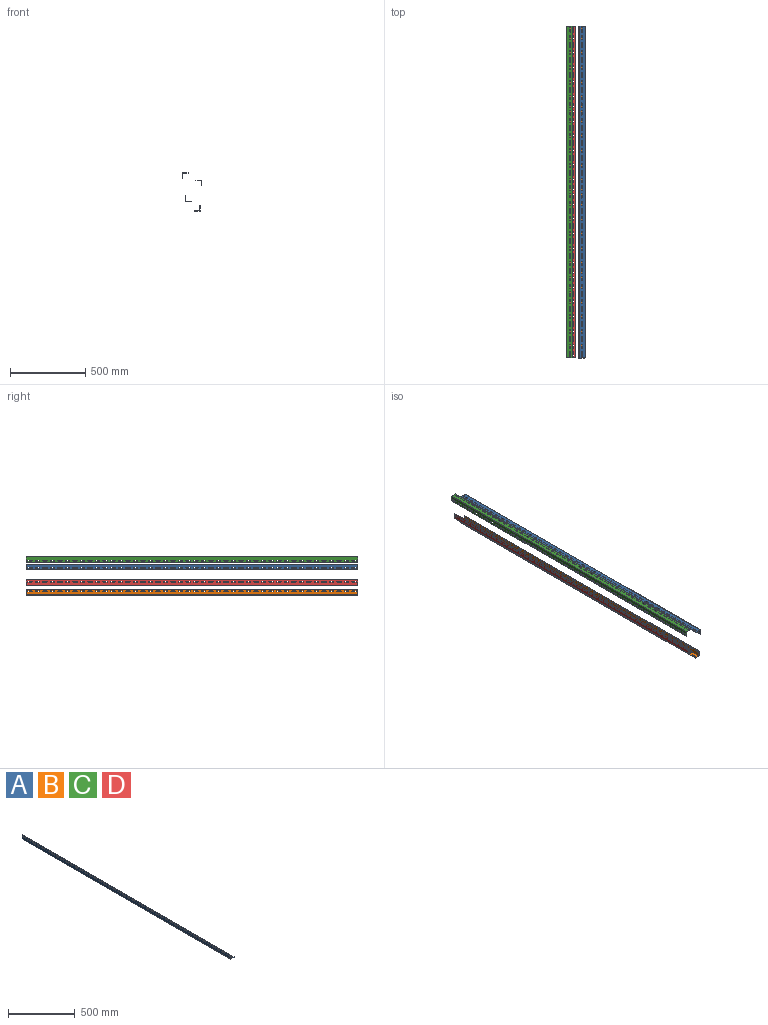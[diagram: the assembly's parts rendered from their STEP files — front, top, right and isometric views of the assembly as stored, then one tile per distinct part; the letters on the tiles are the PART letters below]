
ASSEMBLY  parts=4 mates=3
PART A: 360 faces, bbox 38.1x2200x38.1 mm
  f0: plane 2200x38.1mm, normal (-1,0,0), area 76239.9mm2, adj f1,f5,f6,f7,f184,f185,f186,f187
  f1: plane 2200x38.1mm, normal (0,0,-1), area 76239.9mm2, adj f0,f2,f6,f7,f8,f9,f10,f11
  f2: plane 2200x2mm, normal (1,0,0), area 4400mm2, adj f1,f3,f6,f7
  f3: plane 2200x36.1mm, normal (0,0,1), area 71839.9mm2, adj f2,f4,f6,f7,f8,f9,f10,f11
  f4: plane 2200x36.1mm, normal (1,0,0), area 71839.9mm2, adj f3,f5,f6,f7,f184,f185,f186,f187
  f5: plane 2200x2mm, normal (0,0,1), area 4400mm2, adj f0,f4,f6,f7
  f6: plane 38.1x38.1mm, normal (0,1,0), area 148.4mm2, adj f0,f1,f2,f3,f4,f5
  f7: plane 38.1x38.1mm, normal (0,-1,0), area 148.4mm2, adj f0,f1,f2,f3,f4,f5
  f8: cylinder r=3mm len=6mm, axis (0,0,1), area 18.8mm2, adj f1,f3,f9,f10
  f9: plane 24x2mm, normal (-1,0,0), area 48mm2, adj f1,f3,f8,f11
  f10: plane 24x2mm, normal (1,0,0), area 48mm2, adj f1,f3,f8,f11
  f11: cylinder r=3mm len=6mm, axis (0,0,1), area 18.8mm2, adj f1,f3,f9,f10
  f12: cylinder r=3mm len=6mm, axis (0,0,1), area 18.8mm2, adj f1,f3,f13,f14
  f13: plane 24x2mm, normal (-1,0,0), area 48mm2, adj f1,f3,f12,f15
  f14: plane 24x2mm, normal (1,0,0), area 48mm2, adj f1,f3,f12,f15
  f15: cylinder r=3mm len=6mm, axis (0,0,1), area 18.8mm2, adj f1,f3,f13,f14
  f16: cylinder r=3mm len=6mm, axis (0,0,1), area 18.8mm2, adj f1,f3,f17,f18
  f17: plane 24x2mm, normal (-1,0,0), area 48mm2, adj f1,f3,f16,f19
  f18: plane 24x2mm, normal (1,0,0), area 48mm2, adj f1,f3,f16,f19
  f19: cylinder r=3mm len=6mm, axis (0,0,1), area 18.8mm2, adj f1,f3,f17,f18
  f20: cylinder r=3mm len=6mm, axis (0,0,1), area 18.8mm2, adj f1,f3,f21,f22
  f21: plane 24x2mm, normal (-1,0,0), area 48mm2, adj f1,f3,f20,f23
  f22: plane 24x2mm, normal (1,0,0), area 48mm2, adj f1,f3,f20,f23
  f23: cylinder r=3mm len=6mm, axis (0,0,1), area 18.8mm2, adj f1,f3,f21,f22
  f24: cylinder r=3mm len=6mm, axis (0,0,1), area 18.8mm2, adj f1,f3,f25,f26
  f25: plane 24x2mm, normal (-1,0,0), area 48mm2, adj f1,f3,f24,f27
  f26: plane 24x2mm, normal (1,0,0), area 48mm2, adj f1,f3,f24,f27
  f27: cylinder r=3mm len=6mm, axis (0,0,1), area 18.8mm2, adj f1,f3,f25,f26
  f28: cylinder r=3mm len=6mm, axis (0,0,1), area 18.8mm2, adj f1,f3,f29,f30
  f29: plane 24x2mm, normal (-1,0,0), area 48mm2, adj f1,f3,f28,f31
  f30: plane 24x2mm, normal (1,0,0), area 48mm2, adj f1,f3,f28,f31
  f31: cylinder r=3mm len=6mm, axis (0,0,1), area 18.8mm2, adj f1,f3,f29,f30
  f32: cylinder r=3mm len=6mm, axis (0,0,1), area 18.8mm2, adj f1,f3,f33,f34
  f33: plane 24x2mm, normal (-1,0,0), area 48mm2, adj f1,f3,f32,f35
  f34: plane 24x2mm, normal (1,0,0), area 48mm2, adj f1,f3,f32,f35
  f35: cylinder r=3mm len=6mm, axis (0,0,1), area 18.8mm2, adj f1,f3,f33,f34
  f36: cylinder r=3mm len=6mm, axis (0,0,1), area 18.8mm2, adj f1,f3,f37,f38
  f37: plane 24x2mm, normal (-1,0,0), area 48mm2, adj f1,f3,f36,f39
  f38: plane 24x2mm, normal (1,0,0), area 48mm2, adj f1,f3,f36,f39
  f39: cylinder r=3mm len=6mm, axis (0,0,1), area 18.8mm2, adj f1,f3,f37,f38
  f40: cylinder r=3mm len=6mm, axis (0,0,1), area 18.8mm2, adj f1,f3,f41,f42
  f41: plane 24x2mm, normal (-1,0,0), area 48mm2, adj f1,f3,f40,f43
  f42: plane 24x2mm, normal (1,0,0), area 48mm2, adj f1,f3,f40,f43
  f43: cylinder r=3mm len=6mm, axis (0,0,1), area 18.8mm2, adj f1,f3,f41,f42
  f44: cylinder r=3mm len=6mm, axis (0,0,1), area 18.8mm2, adj f1,f3,f45,f46
  f45: plane 24x2mm, normal (-1,0,0), area 48mm2, adj f1,f3,f44,f47
  f46: plane 24x2mm, normal (1,0,0), area 48mm2, adj f1,f3,f44,f47
  f47: cylinder r=3mm len=6mm, axis (0,0,1), area 18.8mm2, adj f1,f3,f45,f46
  f48: cylinder r=3mm len=6mm, axis (0,0,1), area 18.8mm2, adj f1,f3,f49,f50
  f49: plane 24x2mm, normal (-1,0,0), area 48mm2, adj f1,f3,f48,f51
  f50: plane 24x2mm, normal (1,0,0), area 48mm2, adj f1,f3,f48,f51
  f51: cylinder r=3mm len=6mm, axis (0,0,1), area 18.8mm2, adj f1,f3,f49,f50
  f52: cylinder r=3mm len=6mm, axis (0,0,1), area 18.8mm2, adj f1,f3,f53,f54
  f53: plane 24x2mm, normal (-1,0,0), area 48mm2, adj f1,f3,f52,f55
  f54: plane 24x2mm, normal (1,0,0), area 48mm2, adj f1,f3,f52,f55
  f55: cylinder r=3mm len=6mm, axis (0,0,1), area 18.8mm2, adj f1,f3,f53,f54
  f56: cylinder r=3mm len=6mm, axis (0,0,1), area 18.8mm2, adj f1,f3,f57,f58
  f57: plane 24x2mm, normal (-1,0,0), area 48mm2, adj f1,f3,f56,f59
  f58: plane 24x2mm, normal (1,0,0), area 48mm2, adj f1,f3,f56,f59
  f59: cylinder r=3mm len=6mm, axis (0,0,1), area 18.8mm2, adj f1,f3,f57,f58
  f60: cylinder r=3mm len=6mm, axis (0,0,1), area 18.8mm2, adj f1,f3,f61,f62
  f61: plane 24x2mm, normal (-1,0,0), area 48mm2, adj f1,f3,f60,f63
  f62: plane 24x2mm, normal (1,0,0), area 48mm2, adj f1,f3,f60,f63
  f63: cylinder r=3mm len=6mm, axis (0,0,1), area 18.8mm2, adj f1,f3,f61,f62
  f64: cylinder r=3mm len=6mm, axis (0,0,1), area 18.8mm2, adj f1,f3,f65,f66
  f65: plane 24x2mm, normal (-1,0,0), area 48mm2, adj f1,f3,f64,f67
  f66: plane 24x2mm, normal (1,0,0), area 48mm2, adj f1,f3,f64,f67
  f67: cylinder r=3mm len=6mm, axis (0,0,1), area 18.8mm2, adj f1,f3,f65,f66
  f68: cylinder r=3mm len=6mm, axis (0,0,1), area 18.8mm2, adj f1,f3,f69,f70
  f69: plane 24x2mm, normal (-1,0,0), area 48mm2, adj f1,f3,f68,f71
  f70: plane 24x2mm, normal (1,0,0), area 48mm2, adj f1,f3,f68,f71
  f71: cylinder r=3mm len=6mm, axis (0,0,1), area 18.8mm2, adj f1,f3,f69,f70
  f72: cylinder r=3mm len=6mm, axis (0,0,1), area 18.8mm2, adj f1,f3,f73,f74
  f73: plane 24x2mm, normal (-1,0,0), area 48mm2, adj f1,f3,f72,f75
  f74: plane 24x2mm, normal (1,0,0), area 48mm2, adj f1,f3,f72,f75
  f75: cylinder r=3mm len=6mm, axis (0,0,1), area 18.8mm2, adj f1,f3,f73,f74
  f76: cylinder r=3mm len=6mm, axis (0,0,1), area 18.8mm2, adj f1,f3,f77,f78
  f77: plane 24x2mm, normal (-1,0,0), area 48mm2, adj f1,f3,f76,f79
  f78: plane 24x2mm, normal (1,0,0), area 48mm2, adj f1,f3,f76,f79
  f79: cylinder r=3mm len=6mm, axis (0,0,1), area 18.8mm2, adj f1,f3,f77,f78
  f80: cylinder r=3mm len=6mm, axis (0,0,1), area 18.8mm2, adj f1,f3,f81,f82
  f81: plane 24x2mm, normal (-1,0,0), area 48mm2, adj f1,f3,f80,f83
  f82: plane 24x2mm, normal (1,0,0), area 48mm2, adj f1,f3,f80,f83
  f83: cylinder r=3mm len=6mm, axis (0,0,1), area 18.8mm2, adj f1,f3,f81,f82
  f84: cylinder r=3mm len=6mm, axis (0,0,1), area 18.8mm2, adj f1,f3,f85,f86
  f85: plane 24x2mm, normal (-1,0,0), area 48mm2, adj f1,f3,f84,f87
  f86: plane 24x2mm, normal (1,0,0), area 48mm2, adj f1,f3,f84,f87
  f87: cylinder r=3mm len=6mm, axis (0,0,1), area 18.8mm2, adj f1,f3,f85,f86
  f88: cylinder r=3mm len=6mm, axis (0,0,1), area 18.8mm2, adj f1,f3,f89,f90
  f89: plane 24x2mm, normal (-1,0,0), area 48mm2, adj f1,f3,f88,f91
  f90: plane 24x2mm, normal (1,0,0), area 48mm2, adj f1,f3,f88,f91
  f91: cylinder r=3mm len=6mm, axis (0,0,1), area 18.8mm2, adj f1,f3,f89,f90
  f92: cylinder r=3mm len=6mm, axis (0,0,1), area 18.8mm2, adj f1,f3,f93,f94
  f93: plane 24x2mm, normal (-1,0,0), area 48mm2, adj f1,f3,f92,f95
  f94: plane 24x2mm, normal (1,0,0), area 48mm2, adj f1,f3,f92,f95
  f95: cylinder r=3mm len=6mm, axis (0,0,1), area 18.8mm2, adj f1,f3,f93,f94
  f96: cylinder r=3mm len=6mm, axis (0,0,1), area 18.8mm2, adj f1,f3,f97,f98
  f97: plane 24x2mm, normal (-1,0,0), area 48mm2, adj f1,f3,f96,f99
  f98: plane 24x2mm, normal (1,0,0), area 48mm2, adj f1,f3,f96,f99
  f99: cylinder r=3mm len=6mm, axis (0,0,1), area 18.8mm2, adj f1,f3,f97,f98
  f100: cylinder r=3mm len=6mm, axis (0,0,1), area 18.8mm2, adj f1,f3,f101,f102
  f101: plane 24x2mm, normal (-1,0,0), area 48mm2, adj f1,f3,f100,f103
  f102: plane 24x2mm, normal (1,0,0), area 48mm2, adj f1,f3,f100,f103
  f103: cylinder r=3mm len=6mm, axis (0,0,1), area 18.8mm2, adj f1,f3,f101,f102
  f104: cylinder r=3mm len=6mm, axis (0,0,1), area 18.8mm2, adj f1,f3,f105,f106
  f105: plane 24x2mm, normal (-1,0,0), area 48mm2, adj f1,f3,f104,f107
  f106: plane 24x2mm, normal (1,0,0), area 48mm2, adj f1,f3,f104,f107
  f107: cylinder r=3mm len=6mm, axis (0,0,1), area 18.8mm2, adj f1,f3,f105,f106
  f108: cylinder r=3mm len=6mm, axis (0,0,1), area 18.8mm2, adj f1,f3,f109,f110
  f109: plane 24x2mm, normal (-1,0,0), area 48mm2, adj f1,f3,f108,f111
  f110: plane 24x2mm, normal (1,0,0), area 48mm2, adj f1,f3,f108,f111
  f111: cylinder r=3mm len=6mm, axis (0,0,1), area 18.8mm2, adj f1,f3,f109,f110
  f112: cylinder r=3mm len=6mm, axis (0,0,1), area 18.8mm2, adj f1,f3,f113,f114
  f113: plane 24x2mm, normal (-1,0,0), area 48mm2, adj f1,f3,f112,f115
  f114: plane 24x2mm, normal (1,0,0), area 48mm2, adj f1,f3,f112,f115
  f115: cylinder r=3mm len=6mm, axis (0,0,1), area 18.8mm2, adj f1,f3,f113,f114
  f116: cylinder r=3mm len=6mm, axis (0,0,1), area 18.8mm2, adj f1,f3,f117,f118
  f117: plane 24x2mm, normal (-1,0,0), area 48mm2, adj f1,f3,f116,f119
  f118: plane 24x2mm, normal (1,0,0), area 48mm2, adj f1,f3,f116,f119
  f119: cylinder r=3mm len=6mm, axis (0,0,1), area 18.8mm2, adj f1,f3,f117,f118
  f120: cylinder r=3mm len=6mm, axis (0,0,1), area 18.8mm2, adj f1,f3,f121,f122
  f121: plane 24x2mm, normal (-1,0,0), area 48mm2, adj f1,f3,f120,f123
  f122: plane 24x2mm, normal (1,0,0), area 48mm2, adj f1,f3,f120,f123
  f123: cylinder r=3mm len=6mm, axis (0,0,1), area 18.8mm2, adj f1,f3,f121,f122
  f124: cylinder r=3mm len=6mm, axis (0,0,1), area 18.8mm2, adj f1,f3,f125,f126
  f125: plane 24x2mm, normal (-1,0,0), area 48mm2, adj f1,f3,f124,f127
  f126: plane 24x2mm, normal (1,0,0), area 48mm2, adj f1,f3,f124,f127
  f127: cylinder r=3mm len=6mm, axis (0,0,1), area 18.8mm2, adj f1,f3,f125,f126
  f128: cylinder r=3mm len=6mm, axis (0,0,1), area 18.8mm2, adj f1,f3,f129,f130
  f129: plane 24x2mm, normal (-1,0,0), area 48mm2, adj f1,f3,f128,f131
  f130: plane 24x2mm, normal (1,0,0), area 48mm2, adj f1,f3,f128,f131
  f131: cylinder r=3mm len=6mm, axis (0,0,1), area 18.8mm2, adj f1,f3,f129,f130
  f132: cylinder r=3mm len=6mm, axis (0,0,1), area 18.8mm2, adj f1,f3,f133,f134
  f133: plane 24x2mm, normal (-1,0,0), area 48mm2, adj f1,f3,f132,f135
  f134: plane 24x2mm, normal (1,0,0), area 48mm2, adj f1,f3,f132,f135
  f135: cylinder r=3mm len=6mm, axis (0,0,1), area 18.8mm2, adj f1,f3,f133,f134
  f136: cylinder r=3mm len=6mm, axis (0,0,1), area 18.8mm2, adj f1,f3,f137,f138
  f137: plane 24x2mm, normal (-1,0,0), area 48mm2, adj f1,f3,f136,f139
  f138: plane 24x2mm, normal (1,0,0), area 48mm2, adj f1,f3,f136,f139
  f139: cylinder r=3mm len=6mm, axis (0,0,1), area 18.8mm2, adj f1,f3,f137,f138
  f140: cylinder r=3mm len=6mm, axis (0,0,1), area 18.8mm2, adj f1,f3,f141,f142
  f141: plane 24x2mm, normal (-1,0,0), area 48mm2, adj f1,f3,f140,f143
  f142: plane 24x2mm, normal (1,0,0), area 48mm2, adj f1,f3,f140,f143
  f143: cylinder r=3mm len=6mm, axis (0,0,1), area 18.8mm2, adj f1,f3,f141,f142
  f144: cylinder r=3mm len=6mm, axis (0,0,1), area 18.8mm2, adj f1,f3,f145,f146
  f145: plane 24x2mm, normal (-1,0,0), area 48mm2, adj f1,f3,f144,f147
  f146: plane 24x2mm, normal (1,0,0), area 48mm2, adj f1,f3,f144,f147
  f147: cylinder r=3mm len=6mm, axis (0,0,1), area 18.8mm2, adj f1,f3,f145,f146
  f148: cylinder r=3mm len=6mm, axis (0,0,1), area 18.8mm2, adj f1,f3,f149,f150
  f149: plane 24x2mm, normal (-1,0,0), area 48mm2, adj f1,f3,f148,f151
  f150: plane 24x2mm, normal (1,0,0), area 48mm2, adj f1,f3,f148,f151
  f151: cylinder r=3mm len=6mm, axis (0,0,1), area 18.8mm2, adj f1,f3,f149,f150
  f152: cylinder r=3mm len=6mm, axis (0,0,1), area 18.8mm2, adj f1,f3,f153,f154
  f153: plane 24x2mm, normal (-1,0,0), area 48mm2, adj f1,f3,f152,f155
  f154: plane 24x2mm, normal (1,0,0), area 48mm2, adj f1,f3,f152,f155
  f155: cylinder r=3mm len=6mm, axis (0,0,1), area 18.8mm2, adj f1,f3,f153,f154
  f156: cylinder r=3mm len=6mm, axis (0,0,1), area 18.8mm2, adj f1,f3,f157,f158
  f157: plane 24x2mm, normal (-1,0,0), area 48mm2, adj f1,f3,f156,f159
  f158: plane 24x2mm, normal (1,0,0), area 48mm2, adj f1,f3,f156,f159
  f159: cylinder r=3mm len=6mm, axis (0,0,1), area 18.8mm2, adj f1,f3,f157,f158
  f160: cylinder r=3mm len=6mm, axis (0,0,1), area 18.8mm2, adj f1,f3,f161,f162
  f161: plane 24x2mm, normal (-1,0,0), area 48mm2, adj f1,f3,f160,f163
  f162: plane 24x2mm, normal (1,0,0), area 48mm2, adj f1,f3,f160,f163
  f163: cylinder r=3mm len=6mm, axis (0,0,1), area 18.8mm2, adj f1,f3,f161,f162
  f164: cylinder r=3mm len=6mm, axis (0,0,1), area 18.8mm2, adj f1,f3,f165,f166
  f165: plane 24x2mm, normal (-1,0,0), area 48mm2, adj f1,f3,f164,f167
  f166: plane 24x2mm, normal (1,0,0), area 48mm2, adj f1,f3,f164,f167
  f167: cylinder r=3mm len=6mm, axis (0,0,1), area 18.8mm2, adj f1,f3,f165,f166
  f168: cylinder r=3mm len=6mm, axis (0,0,1), area 18.8mm2, adj f1,f3,f169,f170
  f169: plane 24x2mm, normal (-1,0,0), area 48mm2, adj f1,f3,f168,f171
  f170: plane 24x2mm, normal (1,0,0), area 48mm2, adj f1,f3,f168,f171
  f171: cylinder r=3mm len=6mm, axis (0,0,1), area 18.8mm2, adj f1,f3,f169,f170
  f172: cylinder r=3mm len=6mm, axis (0,0,1), area 18.8mm2, adj f1,f3,f173,f174
  f173: plane 24x2mm, normal (-1,0,0), area 48mm2, adj f1,f3,f172,f175
  f174: plane 24x2mm, normal (1,0,0), area 48mm2, adj f1,f3,f172,f175
  f175: cylinder r=3mm len=6mm, axis (0,0,1), area 18.8mm2, adj f1,f3,f173,f174
  f176: cylinder r=3mm len=6mm, axis (0,0,1), area 18.8mm2, adj f1,f3,f177,f178
  f177: plane 24x2mm, normal (-1,0,0), area 48mm2, adj f1,f3,f176,f179
  f178: plane 24x2mm, normal (1,0,0), area 48mm2, adj f1,f3,f176,f179
  f179: cylinder r=3mm len=6mm, axis (0,0,1), area 18.8mm2, adj f1,f3,f177,f178
  f180: cylinder r=3mm len=6mm, axis (0,0,1), area 18.8mm2, adj f1,f3,f181,f182
  f181: plane 24x2mm, normal (-1,0,0), area 48mm2, adj f1,f3,f180,f183
  f182: plane 24x2mm, normal (1,0,0), area 48mm2, adj f1,f3,f180,f183
  f183: cylinder r=3mm len=6mm, axis (0,0,1), area 18.8mm2, adj f1,f3,f181,f182
  f184: cylinder r=3mm len=6mm, axis (1,0,0), area 18.8mm2, adj f0,f4,f185,f186
  f185: plane 24x2mm, normal (0,0,1), area 48mm2, adj f0,f4,f184,f187
  f186: plane 24x2mm, normal (0,0,-1), area 48mm2, adj f0,f4,f184,f187
  f187: cylinder r=3mm len=6mm, axis (1,0,0), area 18.8mm2, adj f0,f4,f185,f186
  f188: cylinder r=3mm len=6mm, axis (1,0,0), area 18.8mm2, adj f0,f4,f189,f190
  f189: plane 24x2mm, normal (0,0,1), area 48mm2, adj f0,f4,f188,f191
  f190: plane 24x2mm, normal (0,0,-1), area 48mm2, adj f0,f4,f188,f191
  f191: cylinder r=3mm len=6mm, axis (1,0,0), area 18.8mm2, adj f0,f4,f189,f190
  f192: cylinder r=3mm len=6mm, axis (1,0,0), area 18.8mm2, adj f0,f4,f193,f194
  f193: plane 24x2mm, normal (0,0,1), area 48mm2, adj f0,f4,f192,f195
  f194: plane 24x2mm, normal (0,0,-1), area 48mm2, adj f0,f4,f192,f195
  f195: cylinder r=3mm len=6mm, axis (1,0,0), area 18.8mm2, adj f0,f4,f193,f194
  f196: cylinder r=3mm len=6mm, axis (1,0,0), area 18.8mm2, adj f0,f4,f197,f198
  f197: plane 24x2mm, normal (0,0,1), area 48mm2, adj f0,f4,f196,f199
  f198: plane 24x2mm, normal (0,0,-1), area 48mm2, adj f0,f4,f196,f199
  f199: cylinder r=3mm len=6mm, axis (1,0,0), area 18.8mm2, adj f0,f4,f197,f198
  f200: cylinder r=3mm len=6mm, axis (1,0,0), area 18.8mm2, adj f0,f4,f201,f202
  f201: plane 24x2mm, normal (0,0,1), area 48mm2, adj f0,f4,f200,f203
  f202: plane 24x2mm, normal (0,0,-1), area 48mm2, adj f0,f4,f200,f203
  f203: cylinder r=3mm len=6mm, axis (1,0,0), area 18.8mm2, adj f0,f4,f201,f202
  f204: cylinder r=3mm len=6mm, axis (1,0,0), area 18.8mm2, adj f0,f4,f205,f206
  f205: plane 24x2mm, normal (0,0,1), area 48mm2, adj f0,f4,f204,f207
  f206: plane 24x2mm, normal (0,0,-1), area 48mm2, adj f0,f4,f204,f207
  f207: cylinder r=3mm len=6mm, axis (1,0,0), area 18.8mm2, adj f0,f4,f205,f206
  f208: cylinder r=3mm len=6mm, axis (1,0,0), area 18.8mm2, adj f0,f4,f209,f210
  f209: plane 24x2mm, normal (0,0,1), area 48mm2, adj f0,f4,f208,f211
  f210: plane 24x2mm, normal (0,0,-1), area 48mm2, adj f0,f4,f208,f211
  f211: cylinder r=3mm len=6mm, axis (1,0,0), area 18.8mm2, adj f0,f4,f209,f210
  f212: cylinder r=3mm len=6mm, axis (1,0,0), area 18.8mm2, adj f0,f4,f213,f214
  f213: plane 24x2mm, normal (0,0,1), area 48mm2, adj f0,f4,f212,f215
  f214: plane 24x2mm, normal (0,0,-1), area 48mm2, adj f0,f4,f212,f215
  f215: cylinder r=3mm len=6mm, axis (1,0,0), area 18.8mm2, adj f0,f4,f213,f214
  f216: cylinder r=3mm len=6mm, axis (1,0,0), area 18.8mm2, adj f0,f4,f217,f218
  f217: plane 24x2mm, normal (0,0,1), area 48mm2, adj f0,f4,f216,f219
  f218: plane 24x2mm, normal (0,0,-1), area 48mm2, adj f0,f4,f216,f219
  f219: cylinder r=3mm len=6mm, axis (1,0,0), area 18.8mm2, adj f0,f4,f217,f218
  f220: cylinder r=3mm len=6mm, axis (1,0,0), area 18.8mm2, adj f0,f4,f221,f222
  f221: plane 24x2mm, normal (0,0,1), area 48mm2, adj f0,f4,f220,f223
  f222: plane 24x2mm, normal (0,0,-1), area 48mm2, adj f0,f4,f220,f223
  f223: cylinder r=3mm len=6mm, axis (1,0,0), area 18.8mm2, adj f0,f4,f221,f222
  f224: cylinder r=3mm len=6mm, axis (1,0,0), area 18.8mm2, adj f0,f4,f225,f226
  f225: plane 24x2mm, normal (0,0,1), area 48mm2, adj f0,f4,f224,f227
  f226: plane 24x2mm, normal (0,0,-1), area 48mm2, adj f0,f4,f224,f227
  f227: cylinder r=3mm len=6mm, axis (1,0,0), area 18.8mm2, adj f0,f4,f225,f226
  f228: cylinder r=3mm len=6mm, axis (1,0,0), area 18.8mm2, adj f0,f4,f229,f230
  f229: plane 24x2mm, normal (0,0,1), area 48mm2, adj f0,f4,f228,f231
  f230: plane 24x2mm, normal (0,0,-1), area 48mm2, adj f0,f4,f228,f231
  f231: cylinder r=3mm len=6mm, axis (1,0,0), area 18.8mm2, adj f0,f4,f229,f230
  f232: cylinder r=3mm len=6mm, axis (1,0,0), area 18.8mm2, adj f0,f4,f233,f234
  f233: plane 24x2mm, normal (0,0,1), area 48mm2, adj f0,f4,f232,f235
  f234: plane 24x2mm, normal (0,0,-1), area 48mm2, adj f0,f4,f232,f235
  f235: cylinder r=3mm len=6mm, axis (1,0,0), area 18.8mm2, adj f0,f4,f233,f234
  f236: cylinder r=3mm len=6mm, axis (1,0,0), area 18.8mm2, adj f0,f4,f237,f238
  f237: plane 24x2mm, normal (0,0,1), area 48mm2, adj f0,f4,f236,f239
  f238: plane 24x2mm, normal (0,0,-1), area 48mm2, adj f0,f4,f236,f239
  f239: cylinder r=3mm len=6mm, axis (1,0,0), area 18.8mm2, adj f0,f4,f237,f238
  f240: cylinder r=3mm len=6mm, axis (1,0,0), area 18.8mm2, adj f0,f4,f241,f242
  f241: plane 24x2mm, normal (0,0,1), area 48mm2, adj f0,f4,f240,f243
  f242: plane 24x2mm, normal (0,0,-1), area 48mm2, adj f0,f4,f240,f243
  f243: cylinder r=3mm len=6mm, axis (1,0,0), area 18.8mm2, adj f0,f4,f241,f242
  f244: cylinder r=3mm len=6mm, axis (1,0,0), area 18.8mm2, adj f0,f4,f245,f246
  f245: plane 24x2mm, normal (0,0,1), area 48mm2, adj f0,f4,f244,f247
  f246: plane 24x2mm, normal (0,0,-1), area 48mm2, adj f0,f4,f244,f247
  f247: cylinder r=3mm len=6mm, axis (1,0,0), area 18.8mm2, adj f0,f4,f245,f246
  f248: cylinder r=3mm len=6mm, axis (1,0,0), area 18.8mm2, adj f0,f4,f249,f250
  f249: plane 24x2mm, normal (0,0,1), area 48mm2, adj f0,f4,f248,f251
  f250: plane 24x2mm, normal (0,0,-1), area 48mm2, adj f0,f4,f248,f251
  f251: cylinder r=3mm len=6mm, axis (1,0,0), area 18.8mm2, adj f0,f4,f249,f250
  f252: cylinder r=3mm len=6mm, axis (1,0,0), area 18.8mm2, adj f0,f4,f253,f254
  f253: plane 24x2mm, normal (0,0,1), area 48mm2, adj f0,f4,f252,f255
  f254: plane 24x2mm, normal (0,0,-1), area 48mm2, adj f0,f4,f252,f255
  f255: cylinder r=3mm len=6mm, axis (1,0,0), area 18.8mm2, adj f0,f4,f253,f254
  f256: cylinder r=3mm len=6mm, axis (1,0,0), area 18.8mm2, adj f0,f4,f257,f258
  f257: plane 24x2mm, normal (0,0,1), area 48mm2, adj f0,f4,f256,f259
  f258: plane 24x2mm, normal (0,0,-1), area 48mm2, adj f0,f4,f256,f259
  f259: cylinder r=3mm len=6mm, axis (1,0,0), area 18.8mm2, adj f0,f4,f257,f258
  f260: cylinder r=3mm len=6mm, axis (1,0,0), area 18.8mm2, adj f0,f4,f261,f262
  f261: plane 24x2mm, normal (0,0,1), area 48mm2, adj f0,f4,f260,f263
  f262: plane 24x2mm, normal (0,0,-1), area 48mm2, adj f0,f4,f260,f263
  f263: cylinder r=3mm len=6mm, axis (1,0,0), area 18.8mm2, adj f0,f4,f261,f262
  f264: cylinder r=3mm len=6mm, axis (1,0,0), area 18.8mm2, adj f0,f4,f265,f266
  f265: plane 24x2mm, normal (0,0,1), area 48mm2, adj f0,f4,f264,f267
  f266: plane 24x2mm, normal (0,0,-1), area 48mm2, adj f0,f4,f264,f267
  f267: cylinder r=3mm len=6mm, axis (1,0,0), area 18.8mm2, adj f0,f4,f265,f266
  f268: cylinder r=3mm len=6mm, axis (1,0,0), area 18.8mm2, adj f0,f4,f269,f270
  f269: plane 24x2mm, normal (0,0,1), area 48mm2, adj f0,f4,f268,f271
  f270: plane 24x2mm, normal (0,0,-1), area 48mm2, adj f0,f4,f268,f271
  f271: cylinder r=3mm len=6mm, axis (1,0,0), area 18.8mm2, adj f0,f4,f269,f270
  f272: cylinder r=3mm len=6mm, axis (1,0,0), area 18.8mm2, adj f0,f4,f273,f274
  f273: plane 24x2mm, normal (0,0,1), area 48mm2, adj f0,f4,f272,f275
  f274: plane 24x2mm, normal (0,0,-1), area 48mm2, adj f0,f4,f272,f275
  f275: cylinder r=3mm len=6mm, axis (1,0,0), area 18.8mm2, adj f0,f4,f273,f274
  f276: cylinder r=3mm len=6mm, axis (1,0,0), area 18.8mm2, adj f0,f4,f277,f278
  f277: plane 24x2mm, normal (0,0,1), area 48mm2, adj f0,f4,f276,f279
  f278: plane 24x2mm, normal (0,0,-1), area 48mm2, adj f0,f4,f276,f279
  f279: cylinder r=3mm len=6mm, axis (1,0,0), area 18.8mm2, adj f0,f4,f277,f278
  f280: cylinder r=3mm len=6mm, axis (1,0,0), area 18.8mm2, adj f0,f4,f281,f282
  f281: plane 24x2mm, normal (0,0,1), area 48mm2, adj f0,f4,f280,f283
  f282: plane 24x2mm, normal (0,0,-1), area 48mm2, adj f0,f4,f280,f283
  f283: cylinder r=3mm len=6mm, axis (1,0,0), area 18.8mm2, adj f0,f4,f281,f282
  f284: cylinder r=3mm len=6mm, axis (1,0,0), area 18.8mm2, adj f0,f4,f285,f286
  f285: plane 24x2mm, normal (0,0,1), area 48mm2, adj f0,f4,f284,f287
  f286: plane 24x2mm, normal (0,0,-1), area 48mm2, adj f0,f4,f284,f287
  f287: cylinder r=3mm len=6mm, axis (1,0,0), area 18.8mm2, adj f0,f4,f285,f286
  f288: cylinder r=3mm len=6mm, axis (1,0,0), area 18.8mm2, adj f0,f4,f289,f290
  f289: plane 24x2mm, normal (0,0,1), area 48mm2, adj f0,f4,f288,f291
  f290: plane 24x2mm, normal (0,0,-1), area 48mm2, adj f0,f4,f288,f291
  f291: cylinder r=3mm len=6mm, axis (1,0,0), area 18.8mm2, adj f0,f4,f289,f290
  f292: cylinder r=3mm len=6mm, axis (1,0,0), area 18.8mm2, adj f0,f4,f293,f294
  f293: plane 24x2mm, normal (0,0,1), area 48mm2, adj f0,f4,f292,f295
  f294: plane 24x2mm, normal (0,0,-1), area 48mm2, adj f0,f4,f292,f295
  f295: cylinder r=3mm len=6mm, axis (1,0,0), area 18.8mm2, adj f0,f4,f293,f294
  f296: cylinder r=3mm len=6mm, axis (1,0,0), area 18.8mm2, adj f0,f4,f297,f298
  f297: plane 24x2mm, normal (0,0,1), area 48mm2, adj f0,f4,f296,f299
  f298: plane 24x2mm, normal (0,0,-1), area 48mm2, adj f0,f4,f296,f299
  f299: cylinder r=3mm len=6mm, axis (1,0,0), area 18.8mm2, adj f0,f4,f297,f298
  f300: cylinder r=3mm len=6mm, axis (1,0,0), area 18.8mm2, adj f0,f4,f301,f302
  f301: plane 24x2mm, normal (0,0,1), area 48mm2, adj f0,f4,f300,f303
  f302: plane 24x2mm, normal (0,0,-1), area 48mm2, adj f0,f4,f300,f303
  f303: cylinder r=3mm len=6mm, axis (1,0,0), area 18.8mm2, adj f0,f4,f301,f302
  f304: cylinder r=3mm len=6mm, axis (1,0,0), area 18.8mm2, adj f0,f4,f305,f306
  f305: plane 24x2mm, normal (0,0,1), area 48mm2, adj f0,f4,f304,f307
  f306: plane 24x2mm, normal (0,0,-1), area 48mm2, adj f0,f4,f304,f307
  f307: cylinder r=3mm len=6mm, axis (1,0,0), area 18.8mm2, adj f0,f4,f305,f306
  f308: cylinder r=3mm len=6mm, axis (1,0,0), area 18.8mm2, adj f0,f4,f309,f310
  f309: plane 24x2mm, normal (0,0,1), area 48mm2, adj f0,f4,f308,f311
  f310: plane 24x2mm, normal (0,0,-1), area 48mm2, adj f0,f4,f308,f311
  f311: cylinder r=3mm len=6mm, axis (1,0,0), area 18.8mm2, adj f0,f4,f309,f310
  f312: cylinder r=3mm len=6mm, axis (1,0,0), area 18.8mm2, adj f0,f4,f313,f314
  f313: plane 24x2mm, normal (0,0,1), area 48mm2, adj f0,f4,f312,f315
  f314: plane 24x2mm, normal (0,0,-1), area 48mm2, adj f0,f4,f312,f315
  f315: cylinder r=3mm len=6mm, axis (1,0,0), area 18.8mm2, adj f0,f4,f313,f314
  f316: cylinder r=3mm len=6mm, axis (1,0,0), area 18.8mm2, adj f0,f4,f317,f318
  f317: plane 24x2mm, normal (0,0,1), area 48mm2, adj f0,f4,f316,f319
  f318: plane 24x2mm, normal (0,0,-1), area 48mm2, adj f0,f4,f316,f319
  f319: cylinder r=3mm len=6mm, axis (1,0,0), area 18.8mm2, adj f0,f4,f317,f318
  f320: cylinder r=3mm len=6mm, axis (1,0,0), area 18.8mm2, adj f0,f4,f321,f322
  f321: plane 24x2mm, normal (0,0,1), area 48mm2, adj f0,f4,f320,f323
  f322: plane 24x2mm, normal (0,0,-1), area 48mm2, adj f0,f4,f320,f323
  f323: cylinder r=3mm len=6mm, axis (1,0,0), area 18.8mm2, adj f0,f4,f321,f322
  f324: cylinder r=3mm len=6mm, axis (1,0,0), area 18.8mm2, adj f0,f4,f325,f326
  f325: plane 24x2mm, normal (0,0,1), area 48mm2, adj f0,f4,f324,f327
  f326: plane 24x2mm, normal (0,0,-1), area 48mm2, adj f0,f4,f324,f327
  f327: cylinder r=3mm len=6mm, axis (1,0,0), area 18.8mm2, adj f0,f4,f325,f326
  f328: cylinder r=3mm len=6mm, axis (1,0,0), area 18.8mm2, adj f0,f4,f329,f330
  f329: plane 24x2mm, normal (0,0,1), area 48mm2, adj f0,f4,f328,f331
  f330: plane 24x2mm, normal (0,0,-1), area 48mm2, adj f0,f4,f328,f331
  f331: cylinder r=3mm len=6mm, axis (1,0,0), area 18.8mm2, adj f0,f4,f329,f330
  f332: cylinder r=3mm len=6mm, axis (1,0,0), area 18.8mm2, adj f0,f4,f333,f334
  f333: plane 24x2mm, normal (0,0,1), area 48mm2, adj f0,f4,f332,f335
  f334: plane 24x2mm, normal (0,0,-1), area 48mm2, adj f0,f4,f332,f335
  f335: cylinder r=3mm len=6mm, axis (1,0,0), area 18.8mm2, adj f0,f4,f333,f334
  f336: cylinder r=3mm len=6mm, axis (1,0,0), area 18.8mm2, adj f0,f4,f337,f338
  f337: plane 24x2mm, normal (0,0,1), area 48mm2, adj f0,f4,f336,f339
  f338: plane 24x2mm, normal (0,0,-1), area 48mm2, adj f0,f4,f336,f339
  f339: cylinder r=3mm len=6mm, axis (1,0,0), area 18.8mm2, adj f0,f4,f337,f338
  f340: cylinder r=3mm len=6mm, axis (1,0,0), area 18.8mm2, adj f0,f4,f341,f342
  f341: plane 24x2mm, normal (0,0,1), area 48mm2, adj f0,f4,f340,f343
  f342: plane 24x2mm, normal (0,0,-1), area 48mm2, adj f0,f4,f340,f343
  f343: cylinder r=3mm len=6mm, axis (1,0,0), area 18.8mm2, adj f0,f4,f341,f342
  f344: cylinder r=3mm len=6mm, axis (1,0,0), area 18.8mm2, adj f0,f4,f345,f346
  f345: plane 24x2mm, normal (0,0,1), area 48mm2, adj f0,f4,f344,f347
  f346: plane 24x2mm, normal (0,0,-1), area 48mm2, adj f0,f4,f344,f347
  f347: cylinder r=3mm len=6mm, axis (1,0,0), area 18.8mm2, adj f0,f4,f345,f346
  f348: cylinder r=3mm len=6mm, axis (1,0,0), area 18.8mm2, adj f0,f4,f349,f350
  f349: plane 24x2mm, normal (0,0,1), area 48mm2, adj f0,f4,f348,f351
  f350: plane 24x2mm, normal (0,0,-1), area 48mm2, adj f0,f4,f348,f351
  f351: cylinder r=3mm len=6mm, axis (1,0,0), area 18.8mm2, adj f0,f4,f349,f350
  f352: cylinder r=3mm len=6mm, axis (1,0,0), area 18.8mm2, adj f0,f4,f353,f354
  f353: plane 24x2mm, normal (0,0,1), area 48mm2, adj f0,f4,f352,f355
  f354: plane 24x2mm, normal (0,0,-1), area 48mm2, adj f0,f4,f352,f355
  f355: cylinder r=3mm len=6mm, axis (1,0,0), area 18.8mm2, adj f0,f4,f353,f354
  f356: cylinder r=3mm len=6mm, axis (1,0,0), area 18.8mm2, adj f0,f4,f357,f358
  f357: plane 24x2mm, normal (0,0,1), area 48mm2, adj f0,f4,f356,f359
  f358: plane 24x2mm, normal (0,0,-1), area 48mm2, adj f0,f4,f356,f359
  f359: cylinder r=3mm len=6mm, axis (1,0,0), area 18.8mm2, adj f0,f4,f357,f358
PART B: same geometry as A
PART C: same geometry as A
PART D: same geometry as A
PLACE A rot(axis=(0,1,0),180deg) t=(-90.08,-824.93,704.35)mm
PLACE B rot(axis=(0,-1,0),90deg) t=(-100.13,-824.93,497.59)mm
PLACE C rot(axis=(0,1,0),90deg) t=(-218.84,-824.93,752.58)mm
PLACE D rot(axis=(0,-1,0),0deg) t=(-196.48,-824.93,562.25)mm
MATE planar B.f7 <-> A.f7  axis (0,-1,0) through (-110.4,-824.93,507.86)mm
MATE planar A.f7 <-> C.f7  axis (0,-1,0) through (-92.08,-824.93,702.35)mm
MATE planar D.f7 <-> C.f7  axis (0,-1,0) through (-186.21,-824.93,572.52)mm
